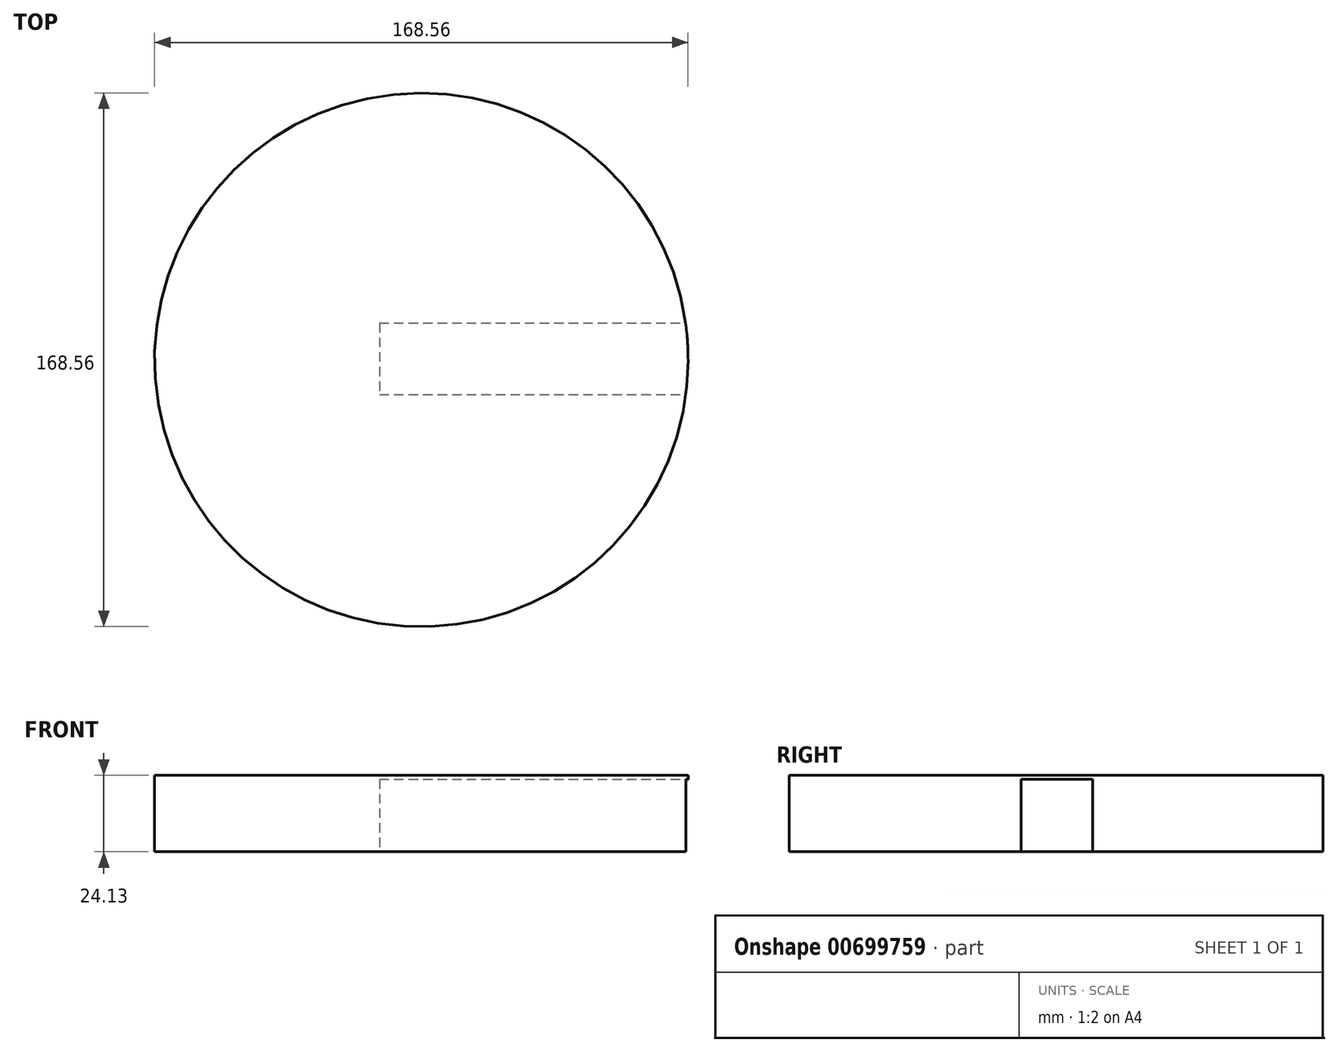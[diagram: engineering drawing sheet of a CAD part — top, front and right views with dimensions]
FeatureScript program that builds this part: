
annotation { "Feature Type Name" : "Feature", "Feature Type Description" : "" }
export const myFeature = defineFeature(function(context is Context, id is Id, definition is map)
    precondition{}
    {
        {
            var Q0;
            Q0=qCreatedBy(makeId("Top.planeOp"),FACE);
            var sketch = newSketch(context, id + "F0", { "sketchPlane" : qUnion([Q0])});
            skCircle(sketch, "E0", {"center": v(0, 0) * mm, "radius": 84.28 * mm});
            skSolve(sketch);
        }
        {
            var Q0;
            Q0 = qSketchRegion(id + "F0", true);
            extrude(context, id + "F1", {"entities" : qUnion([Q0]), "depth" : 24.13 * mm, "offsetDistance" : 25.4 * mm});
        }
        {
            var Q0;
            Q0=qCreatedBy(makeId("Top.planeOp"),FACE);
            var sketch = newSketch(context, id + "F2", { "sketchPlane" : qUnion([Q0])});
            skLineSegment(sketch, "E1.bottom", {"start": v(-13.25, 11.59) * mm, "end": v(84.54, 11.59) * mm});
            skLineSegment(sketch, "E1.top", {"start": v(-13.25, -11.02) * mm, "end": v(84.54, -11.02) * mm});
            skLineSegment(sketch, "E1.left", {"start": v(-13.25, 11.59) * mm, "end": v(-13.25, -11.02) * mm});
            skLineSegment(sketch, "E1.right", {"start": v(84.54, 11.59) * mm, "end": v(84.54, -11.02) * mm});
            skSolve(sketch);
        }
        {
            var Q0;
            Q0 = qSketchRegion(id + "F2", true);
            extrude(context, id + "F3", {"entities" : qUnion([Q0]), "operationType" : NewBodyOperationType.REMOVE, "depth" : 22.86 * mm, "offsetDistance" : 25.4 * mm});
        }
    });
